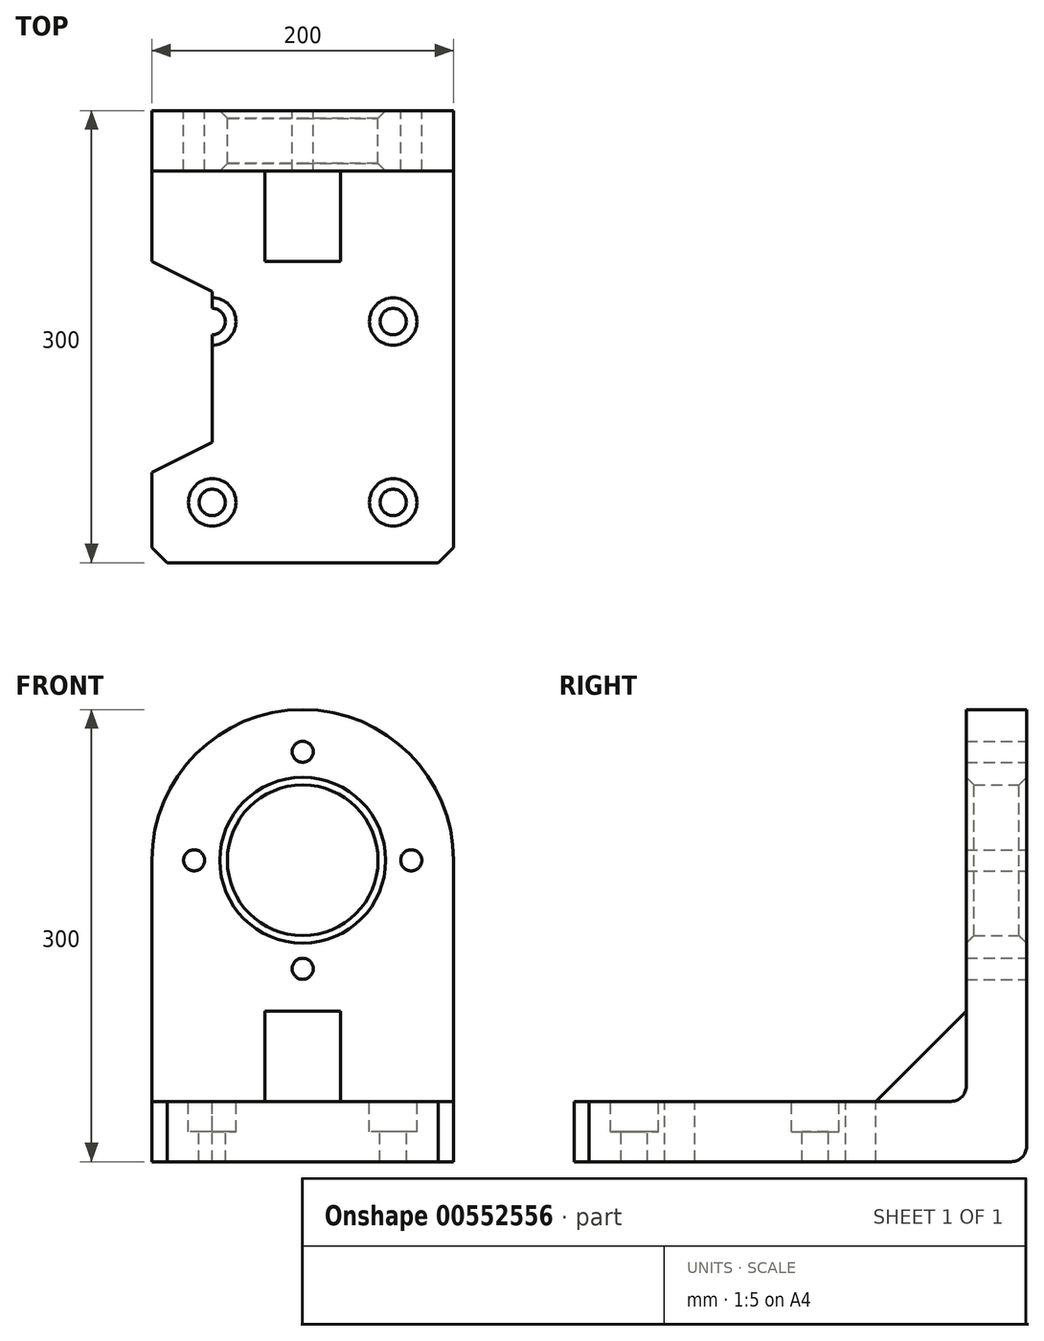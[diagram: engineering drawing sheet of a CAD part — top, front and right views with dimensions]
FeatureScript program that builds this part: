
annotation { "Feature Type Name" : "Feature", "Feature Type Description" : "" }
export const myFeature = defineFeature(function(context is Context, id is Id, definition is map)
    precondition{}
    {
        {
            var Q0;
            Q0=qCreatedBy(makeId("Front.planeOp"),FACE);
            var sketch = newSketch(context, id + "F0", { "sketchPlane" : qUnion([Q0])});
            skLineSegment(sketch, "E0", {"start": v(0, 0) * mm, "end": v(-100, 0) * mm, "construction": true});
            skLineSegment(sketch, "E1.bottom", {"start": v(-100, 0) * mm, "end": v(100, 0) * mm});
            skLineSegment(sketch, "E1.left", {"start": v(-100, 0) * mm, "end": v(-100, 200) * mm});
            skLineSegment(sketch, "E1.right", {"start": v(100, 0) * mm, "end": v(100, 200) * mm});
            skLineSegment(sketch, "E2", {"start": v(0, 0) * mm, "end": v(0, 200) * mm, "construction": true});
            skArc(sketch, "E3", {"start": v(100, 200) * mm, "mid": v(0, 300) * mm, "end": v(-100, 200) * mm});
            skCircle(sketch, "E4", {"center": v(0, 200) * mm, "radius": 50 * mm});
            skCircle(sketch, "E5", {"center": v(0, 200) * mm, "radius": 72 * mm, "construction": true});
            skLineSegment(sketch, "E6", {"start": v(0, 200) * mm, "end": v(0, 300) * mm, "construction": true});
            skLineSegment(sketch, "E7", {"start": v(100, 200) * mm, "end": v(-100, 200) * mm, "construction": true});
            skCircle(sketch, "E8", {"center": v(0, 272) * mm, "radius": 7 * mm});
            skCircle(sketch, "E9", {"center": v(72, 200) * mm, "radius": 7 * mm});
            skCircle(sketch, "E10", {"center": v(0, 128) * mm, "radius": 7 * mm});
            skCircle(sketch, "E11", {"center": v(-72, 200) * mm, "radius": 7 * mm});
            skLineSegment(sketch, "E12", {"start": v(-100, 0) * mm, "end": v(-100, 40) * mm, "construction": true});
            skLineSegment(sketch, "E13", {"start": v(-100, 40) * mm, "end": v(100, 40) * mm});
            skSolve(sketch);
        }
        {
            var Q0;
            Q0 = qSketchRegion(id + "F0", true);
            extrude(context, id + "F1", {"entities" : qUnion([Q0]), "depth" : 40 * mm, "offsetDistance" : 25 * mm});
        }
        {
            var Q0;
            {var subQ0=sQuery(id+"F0.wireOp",EDGE,"E1.bottom");Q0=makeQuery(id+"F0.imprint","IMPRINT",FACE,{"disambiguationData":[TD([[makeQuery(id+"F0.imprint","IMPRINT",EDGE,{"derivedFrom":subQ0}),1.0]])]});}
            extrude(context, id + "F2", {"entities" : qUnion([Q0]), "operationType" : NewBodyOperationType.ADD, "depth" : 300 * mm, "offsetDistance" : 25 * mm});
        }
        {
            var Q0;
            Q0=makeQuery(id+"F1.opExtrude","CAP_EDGE",EDGE,{"disambiguationData":[OSD([sQuery(id+"F0.wireOp",EDGE,"E4")])],"isStart":false});
            var Q1;
            Q1=makeQuery(id+"F1.opExtrude","CAP_EDGE",EDGE,{"disambiguationData":[OSD([sQuery(id+"F0.wireOp",EDGE,"E4")])],"isStart":true});
            chamfer(context, id + "F3", {"entities" : qUnion([Q0, Q1]), "width" : 5 * mm, "tangentPropagation" : true});
        }
        {
            var Q0;
            Q0=makeQuery(id+"F2.opExtrude","SWEPT_FACE",FACE,{"disambiguationData":[OSD([sQuery(id+"F0.wireOp",EDGE,"E13")])]});
            var sketch = newSketch(context, id + "F4", { "sketchPlane" : qUnion([Q0])});
            skLineSegment(sketch, "E14", {"start": v(-100, -300) * mm, "end": v(-60, -300) * mm, "construction": true});
            skLineSegment(sketch, "E15", {"start": v(-60, -300) * mm, "end": v(-60, -260) * mm, "construction": true});
            skCircle(sketch, "E16", {"center": v(-60, -260) * mm, "radius": 15.75 * mm});
            skLineSegment(sketch, "E17", {"start": v(100, -300) * mm, "end": v(60, -300) * mm, "construction": true});
            skLineSegment(sketch, "E18", {"start": v(60, -300) * mm, "end": v(60, -260) * mm, "construction": true});
            skCircle(sketch, "E19", {"center": v(60, -260) * mm, "radius": 15.75 * mm});
            skLineSegment(sketch, "E20", {"start": v(60, -260) * mm, "end": v(60, -140) * mm, "construction": true});
            skCircle(sketch, "E21", {"center": v(60, -140) * mm, "radius": 15.75 * mm});
            skLineSegment(sketch, "E22", {"start": v(-60, -260) * mm, "end": v(-60, -140) * mm, "construction": true});
            skCircle(sketch, "E23", {"center": v(-60, -140) * mm, "radius": 15.75 * mm});
            skCircle(sketch, "E24", {"center": v(-60, -140) * mm, "radius": 8.75 * mm});
            skCircle(sketch, "E25", {"center": v(-60, -260) * mm, "radius": 8.75 * mm});
            skCircle(sketch, "E26", {"center": v(60, -260) * mm, "radius": 8.75 * mm});
            skCircle(sketch, "E27", {"center": v(60, -140) * mm, "radius": 8.75 * mm});
            skSolve(sketch);
        }
        {
            var Q0;
            Q0=makeQuery(id+"F4.imprint","IMPRINT",FACE,{"disambiguationData":[TD([[makeQuery(id+"F4.imprint","IMPRINT",EDGE,{"derivedFrom":sQuery(id+"F4.wireOp",EDGE,"E27")}),1.0]])]});
            var Q1;
            Q1=makeQuery(id+"F4.imprint","IMPRINT",FACE,{"disambiguationData":[TD([[makeQuery(id+"F4.imprint","IMPRINT",EDGE,{"derivedFrom":sQuery(id+"F4.wireOp",EDGE,"E24")}),1.0]])]});
            var Q2;
            Q2=makeQuery(id+"F4.imprint","IMPRINT",FACE,{"disambiguationData":[TD([[makeQuery(id+"F4.imprint","IMPRINT",EDGE,{"derivedFrom":sQuery(id+"F4.wireOp",EDGE,"E26")}),1.0]])]});
            var Q3;
            Q3=makeQuery(id+"F4.imprint","IMPRINT",FACE,{"disambiguationData":[TD([[makeQuery(id+"F4.imprint","IMPRINT",EDGE,{"derivedFrom":sQuery(id+"F4.wireOp",EDGE,"E25")}),1.0]])]});
            extrude(context, id + "F5", {"entities" : qUnion([Q0, Q1, Q2, Q3]), "operationType" : NewBodyOperationType.REMOVE, "endBound" : BoundingType.THROUGH_ALL, "oppositeDirection" : true, "depth" : 25 * mm, "offsetDistance" : 25 * mm});
        }
        {
            var Q0;
            Q0=makeQuery(id+"F4.imprint","IMPRINT",FACE,{"disambiguationData":[TD([[makeQuery(id+"F4.imprint","IMPRINT",EDGE,{"derivedFrom":sQuery(id+"F4.wireOp",EDGE,"E23")}),1.0]])]});
            var Q1;
            Q1=makeQuery(id+"F4.imprint","IMPRINT",FACE,{"disambiguationData":[TD([[makeQuery(id+"F4.imprint","IMPRINT",EDGE,{"derivedFrom":sQuery(id+"F4.wireOp",EDGE,"E21")}),1.0]])]});
            var Q2;
            Q2=makeQuery(id+"F4.imprint","IMPRINT",FACE,{"disambiguationData":[TD([[makeQuery(id+"F4.imprint","IMPRINT",EDGE,{"derivedFrom":sQuery(id+"F4.wireOp",EDGE,"E19")}),1.0]])]});
            var Q3;
            Q3=makeQuery(id+"F4.imprint","IMPRINT",FACE,{"disambiguationData":[TD([[makeQuery(id+"F4.imprint","IMPRINT",EDGE,{"derivedFrom":sQuery(id+"F4.wireOp",EDGE,"E16")}),1.0]])]});
            extrude(context, id + "F6", {"entities" : qUnion([Q0, Q1, Q2, Q3]), "operationType" : NewBodyOperationType.REMOVE, "oppositeDirection" : true, "depth" : 20 * mm, "offsetDistance" : 25 * mm});
        }
        {
            var Q0;
            Q0=makeQuery(id+"F2.opExtrude","CAP_EDGE",EDGE,{"disambiguationData":[OSD([sQuery(id+"F0.wireOp",EDGE,"E1.left")])],"isStart":false});
            var Q1;
            Q1=makeQuery(id+"F2.opExtrude","CAP_EDGE",EDGE,{"disambiguationData":[OSD([sQuery(id+"F0.wireOp",EDGE,"E1.right")])],"isStart":false});
            chamfer(context, id + "F7", {"entities" : qUnion([Q0, Q1]), "width" : 10 * mm, "tangentPropagation" : true});
        }
        {
            var Q0;
            Q0=makeQuery(id+"F1.opExtrude","CAP_EDGE",EDGE,{"disambiguationData":[OSD([sQuery(id+"F0.wireOp",EDGE,"E1.bottom")])],"isStart":true});
            fillet(context, id + "F8", {"entities" : qUnion([Q0]), "radius" : 10 * mm, "tangentPropagation" : true, "allowEdgeOverflow" : false});
        }
        {
            var Q0;
            Q0=qCreatedBy(makeId("Right.planeOp"),FACE);
            var sketch = newSketch(context, id + "F9", { "sketchPlane" : qUnion([Q0])});
            skPoint(sketch, "E28.0", {"position": v(-40, 40) * mm});
            skLineSegment(sketch, "E29.0", {"start": v(-290, 40) * mm, "end": v(-40, 40) * mm});
            skLineSegment(sketch, "E30", {"start": v(-40, 40) * mm, "end": v(-40, 100) * mm});
            skLineSegment(sketch, "E31", {"start": v(-40, 100) * mm, "end": v(-100, 40) * mm});
            skSolve(sketch);
        }
        {
            var Q0;
            Q0 = qSketchRegion(id + "F9", true);
            extrude(context, id + "F10", {"entities" : qUnion([Q0]), "operationType" : NewBodyOperationType.ADD, "endBound" : BoundingType.SYMMETRIC, "depth" : 50 * mm, "offsetDistance" : 25 * mm});
        }
        {
            var Q0;
            Q0=qCreatedBy(makeId("Top.planeOp"),FACE);
            cPlane(context, id + "F11", {"entities" : qUnion([Q0]), "cplaneType" : CPlaneType.OFFSET, "offset" : 40 * mm, "width" : 150 * mm, "height" : 150 * mm});
        }
        {
            var Q0;
            Q0=qCreatedBy(id+"F11.planeOp",FACE);
            var sketch = newSketch(context, id + "F12", { "sketchPlane" : qUnion([Q0])});
            skLineSegment(sketch, "E32", {"start": v(0, 0) * mm, "end": v(0, -300) * mm, "construction": true});
            skLineSegment(sketch, "E33", {"start": v(0, -300) * mm, "end": v(-100, -300) * mm, "construction": true});
            skLineSegment(sketch, "E34", {"start": v(-100, -300) * mm, "end": v(-100, -240) * mm, "construction": true});
            skLineSegment(sketch, "E35", {"start": v(-100, -240) * mm, "end": v(-60, -240) * mm, "construction": true});
            skLineSegment(sketch, "E36", {"start": v(-60, -240) * mm, "end": v(-60, -220) * mm, "construction": true});
            skLineSegment(sketch, "E37", {"start": v(-100, -240) * mm, "end": v(-100, -100) * mm});
            skLineSegment(sketch, "E38", {"start": v(-100, -100) * mm, "end": v(-60, -100) * mm, "construction": true});
            skLineSegment(sketch, "E39", {"start": v(-60, -100) * mm, "end": v(-60, -120) * mm, "construction": true});
            skLineSegment(sketch, "E40", {"start": v(-100, -100) * mm, "end": v(-60, -120) * mm});
            skLineSegment(sketch, "E41", {"start": v(-60, -220) * mm, "end": v(-100, -240) * mm});
            skLineSegment(sketch, "E42", {"start": v(-60, -220) * mm, "end": v(-60, -120) * mm});
            skSolve(sketch);
        }
        {
            var Q0;
            Q0 = qSketchRegion(id + "F12", true);
            extrude(context, id + "F13", {"entities" : qUnion([Q0]), "operationType" : NewBodyOperationType.REMOVE, "endBound" : BoundingType.THROUGH_ALL, "oppositeDirection" : true, "depth" : 25 * mm, "offsetDistance" : 25 * mm});
        }
        {
            var Q0;
            {var subQ0=makeQuery(id+"F2.opExtrude","SWEPT_FACE",FACE,{"disambiguationData":[OSD([sQuery(id+"F0.wireOp",EDGE,"E13")])]});var subQ1=sQuery(id+"F0.wireOp",EDGE,"E1.right");var subQ2=makeQuery(id+"F1.opExtrude","CAP_FACE",FACE,{"disambiguationData":[OSD([sQuery(id+"F0.wireOp",EDGE,"E1.bottom"),sQuery(id+"F0.wireOp",EDGE,"E1.left"),subQ1,sQuery(id+"F0.wireOp",EDGE,"E3"),sQuery(id+"F0.wireOp",EDGE,"E4"),sQuery(id+"F0.wireOp",EDGE,"E8"),sQuery(id+"F0.wireOp",EDGE,"E9"),sQuery(id+"F0.wireOp",EDGE,"E10"),sQuery(id+"F0.wireOp",EDGE,"E11")])],"isStart":false});Q0=makeQuery(id+"F10.boolean.opBoolean","SPLIT",EDGE,{"disambiguationData":[TD([makeQuery(id+"F1.opExtrude","SWEPT_FACE",FACE,{"disambiguationData":[OSD([subQ1])]})])],"derivedFrom":makeQuery(id+"F2.boolean.opBoolean","INTERSECT",EDGE,{"derivedFrom":[subQ2,subQ0]})});}
            var Q1;
            {var subQ0=makeQuery(id+"F2.opExtrude","SWEPT_FACE",FACE,{"disambiguationData":[OSD([sQuery(id+"F0.wireOp",EDGE,"E13")])]});var subQ1=sQuery(id+"F0.wireOp",EDGE,"E1.left");var subQ2=makeQuery(id+"F1.opExtrude","CAP_FACE",FACE,{"disambiguationData":[OSD([sQuery(id+"F0.wireOp",EDGE,"E1.bottom"),subQ1,sQuery(id+"F0.wireOp",EDGE,"E1.right"),sQuery(id+"F0.wireOp",EDGE,"E3"),sQuery(id+"F0.wireOp",EDGE,"E4"),sQuery(id+"F0.wireOp",EDGE,"E8"),sQuery(id+"F0.wireOp",EDGE,"E9"),sQuery(id+"F0.wireOp",EDGE,"E10"),sQuery(id+"F0.wireOp",EDGE,"E11")])],"isStart":false});Q1=makeQuery(id+"F10.boolean.opBoolean","SPLIT",EDGE,{"disambiguationData":[TD([makeQuery(id+"F1.opExtrude","SWEPT_FACE",FACE,{"disambiguationData":[OSD([subQ1])]})])],"derivedFrom":makeQuery(id+"F2.boolean.opBoolean","INTERSECT",EDGE,{"derivedFrom":[subQ2,subQ0]})});}
            fillet(context, id + "F14", {"entities" : qUnion([Q0, Q1]), "radius" : 10 * mm, "tangentPropagation" : true, "allowEdgeOverflow" : false});
        }
    });
